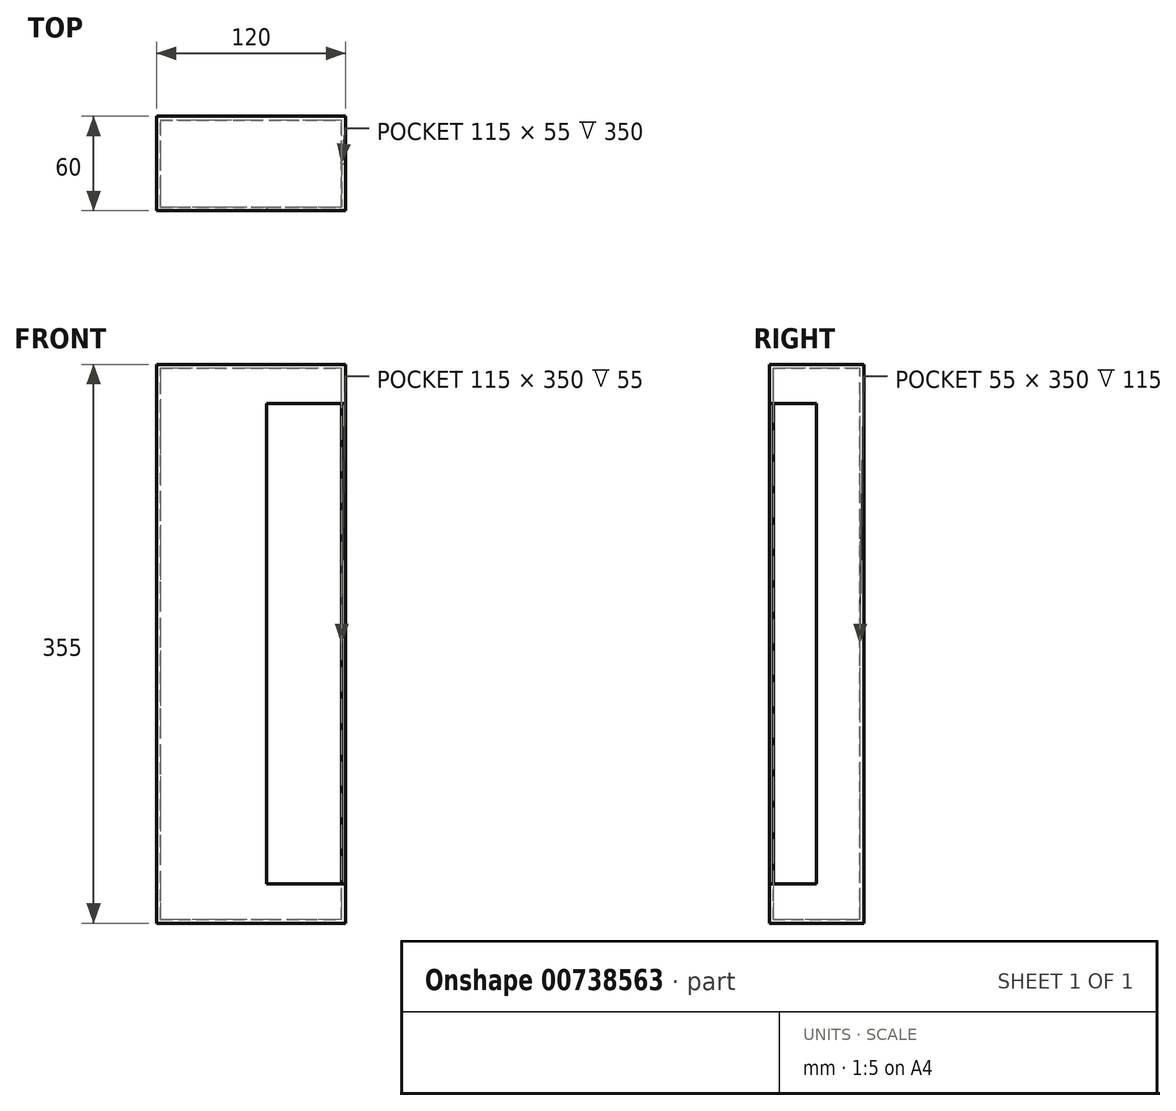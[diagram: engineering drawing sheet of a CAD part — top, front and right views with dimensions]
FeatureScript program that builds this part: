
annotation { "Feature Type Name" : "Feature", "Feature Type Description" : "" }
export const myFeature = defineFeature(function(context is Context, id is Id, definition is map)
    precondition{}
    {
        {
            var Q0;
            Q0=qCreatedBy(makeId("Front.planeOp"),FACE);
            var sketch = newSketch(context, id + "F0", { "sketchPlane" : qUnion([Q0])});
            skLineSegment(sketch, "E0.bottom", {"start": v(0, 0) * mm, "end": v(120, 0) * mm});
            skLineSegment(sketch, "E0.top", {"start": v(0, 355) * mm, "end": v(120, 355) * mm});
            skLineSegment(sketch, "E0.left", {"start": v(0, 0) * mm, "end": v(0, 355) * mm});
            skLineSegment(sketch, "E0.right", {"start": v(120, 0) * mm, "end": v(120, 355) * mm});
            skSolve(sketch);
        }
        {
            var Q0;
            Q0 = qSketchRegion(id + "F0", true);
            extrude(context, id + "F1", {"entities" : qUnion([Q0]), "depth" : 60 * mm, "offsetDistance" : 25 * mm});
        }
        {
            var Q0;
            Q0=makeQuery(id+"F1.opExtrude","CAP_FACE",FACE,{"disambiguationData":[OSD([sQuery(id+"F0.wireOp",EDGE,"E0.bottom"),sQuery(id+"F0.wireOp",EDGE,"E0.top"),sQuery(id+"F0.wireOp",EDGE,"E0.left"),sQuery(id+"F0.wireOp",EDGE,"E0.right")])],"isStart":false});
            var sketch = newSketch(context, id + "F2", { "sketchPlane" : qUnion([Q0])});
            skLineSegment(sketch, "E1.bottom", {"start": v(70, 330) * mm, "end": v(170, 330) * mm});
            skLineSegment(sketch, "E1.top", {"start": v(70, 25) * mm, "end": v(170, 25) * mm});
            skLineSegment(sketch, "E1.left", {"start": v(70, 330) * mm, "end": v(70, 25) * mm});
            skLineSegment(sketch, "E1.right", {"start": v(170, 330) * mm, "end": v(170, 25) * mm});
            skPoint(sketch, "E1.middle", {"position": v(120, 177.5) * mm});
            skSolve(sketch);
        }
        {
            var Q0;
            Q0 = qSketchRegion(id + "F2", true);
            extrude(context, id + "F3", {"entities" : qUnion([Q0]), "operationType" : NewBodyOperationType.REMOVE, "oppositeDirection" : true, "depth" : 30 * mm, "offsetDistance" : 25 * mm});
        }
        {
            var Q0;
            Q0=makeQuery(id+"F3.boolean.opBoolean","COPY",FACE,{"derivedFrom":makeQuery(id+"F3.opExtrude","SWEPT_FACE",FACE,{"disambiguationData":[OSD([sQuery(id+"F2.wireOp",EDGE,"E1.bottom")])]})});
            var Q1;
            Q1=makeQuery(id+"F3.boolean.opBoolean","COPY",FACE,{"derivedFrom":makeQuery(id+"F3.opExtrude","SWEPT_FACE",FACE,{"disambiguationData":[OSD([sQuery(id+"F2.wireOp",EDGE,"E1.left")])]})});
            var Q2;
            Q2=makeQuery(id+"F3.boolean.opBoolean","COPY",FACE,{"derivedFrom":makeQuery(id+"F3.opExtrude","CAP_FACE",FACE,{"disambiguationData":[OSD([sQuery(id+"F2.wireOp",EDGE,"E1.bottom"),sQuery(id+"F2.wireOp",EDGE,"E1.top"),sQuery(id+"F2.wireOp",EDGE,"E1.left"),sQuery(id+"F2.wireOp",EDGE,"E1.right")])],"isStart":false})});
            var Q3;
            Q3=makeQuery(id+"F3.boolean.opBoolean","COPY",FACE,{"derivedFrom":makeQuery(id+"F3.opExtrude","SWEPT_FACE",FACE,{"disambiguationData":[OSD([sQuery(id+"F2.wireOp",EDGE,"E1.top")])]})});
            shell(context, id + "F4", {"entities" : qUnion([Q0, Q1, Q2, Q3]), "thickness" : 2.5 * mm});
        }
    });
